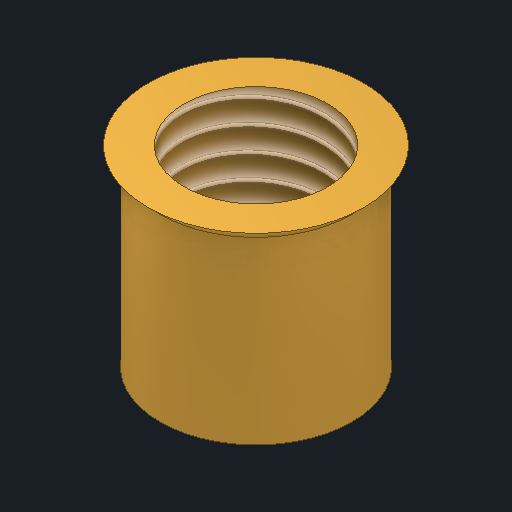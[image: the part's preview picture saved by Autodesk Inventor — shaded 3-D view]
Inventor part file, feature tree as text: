
AUTODESK INVENTOR PART (.ipt)
format: ipt  version: 2024.1 (Build 281209000, 209)  size: 235,520 bytes
history: native  units: mm
features: extrude x2, sketch x2, chamfer x1, thread x1
ambient origin geometry x8: Origin, YZ Plane, XZ Plane, XY Plane, X Axis, Y Axis, Z Axis, Center Point
bodies: Solid1 (feature_tree)
feature tree (6):
  extrude  "Extrusion1"  Depth=4.0mm
  extrude  "Extrusion2"  Depth=4.0mm
  chamfer  "Chamfer1"  Distance=0.25mm
  thread  "Thread1"  [1 undecoded]
  sketch  "Sketch1"  dims[d0=4.0mm d1=3.0mm]
  sketch  "Sketch2"  dims[d2=4.0mm d3=0.0mm d4=4.5mm d5=0.25mm d6=0.0mm d7=0.25mm d8=2.0mm d9=45.0deg d10=4.0mm d11=0.0mm]
note: 1 required parameter value undecoded (feature->parameter linkage not recoverable at this tier; creation-order binding heuristic only, values carry confidence <= 0.55)
